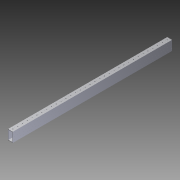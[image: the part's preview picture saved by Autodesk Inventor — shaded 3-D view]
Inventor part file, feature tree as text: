
AUTODESK INVENTOR PART (.ipt)
format: ipt  version: 2014 SP1 (Build 180222100, 222)  size: 739,840 bytes
history: native  units: in
note: dims shown in document units (in); Inventor stores cm internally (conversion verified against a paired STEP export)
features: other x2, extrude x1, imported_body x1, sketch x1
ambient origin geometry x8: Origin, YZ Plane, XZ Plane, XY Plane, X Axis, Y Axis, Z Axis, Center Point
bodies: Body1 (feature_tree)
feature tree (5):
  other  "Cut-Extrude2"
  other  "2x1 Tube1"
  extrude  "Extrusion1"  [1 undecoded]
  imported_body  "Base1"
  sketch  "Sketch1"  dims[d0=26.0in d1=0.0in]
note: 1 required parameter value undecoded (feature->parameter linkage not recoverable at this tier; creation-order binding heuristic only, values carry confidence <= 0.55)
